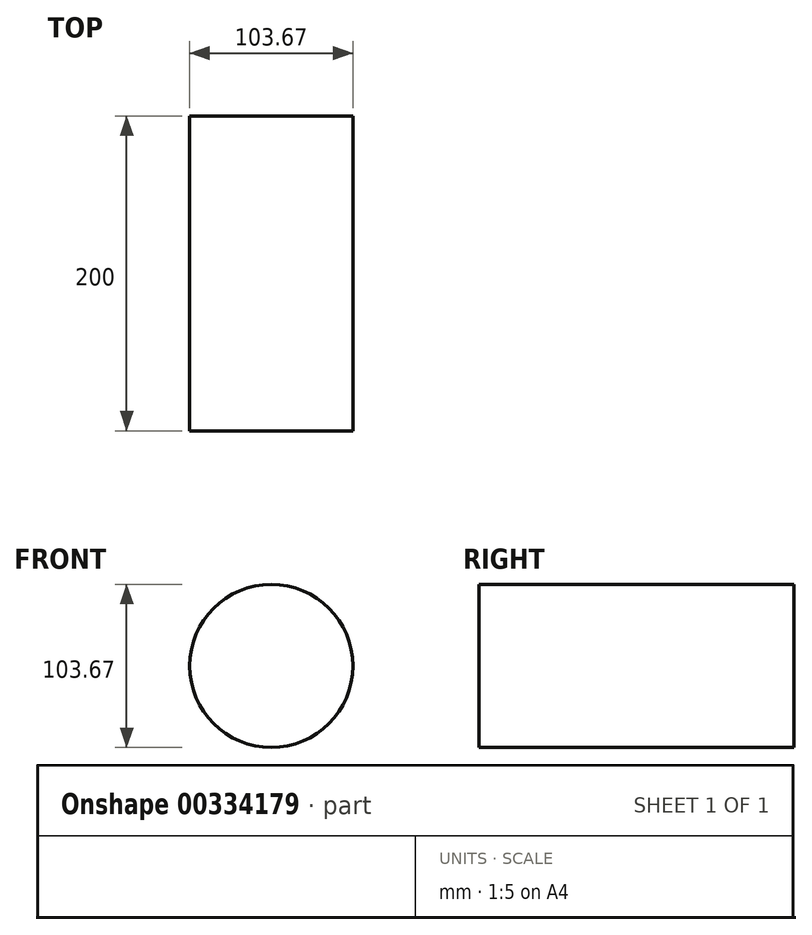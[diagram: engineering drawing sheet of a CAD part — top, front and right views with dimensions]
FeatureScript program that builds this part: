
annotation { "Feature Type Name" : "Feature", "Feature Type Description" : "" }
export const myFeature = defineFeature(function(context is Context, id is Id, definition is map)
    precondition{}
    {
        {
            var Q0;
            Q0=qCreatedBy(makeId("Front.planeOp"),FACE);
            var sketch = newSketch(context, id + "F0", { "sketchPlane" : qUnion([Q0])});
            skCircle(sketch, "E0", {"center": v(-1.1, 2.1) * mm, "radius": 51.83 * mm});
            skSolve(sketch);
        }
        {
            var Q0;
            Q0=makeQuery(id+"F0.imprint","IMPRINT",FACE,{"disambiguationData":[TD([[makeQuery(id+"F0.imprint","IMPRINT",EDGE,{"derivedFrom":sQuery(id+"F0.wireOp",EDGE,"E0")}),1.0]])]});
            extrude(context, id + "F1", {"entities" : qUnion([Q0]), "depth" : 200 * mm});
        }
    });
